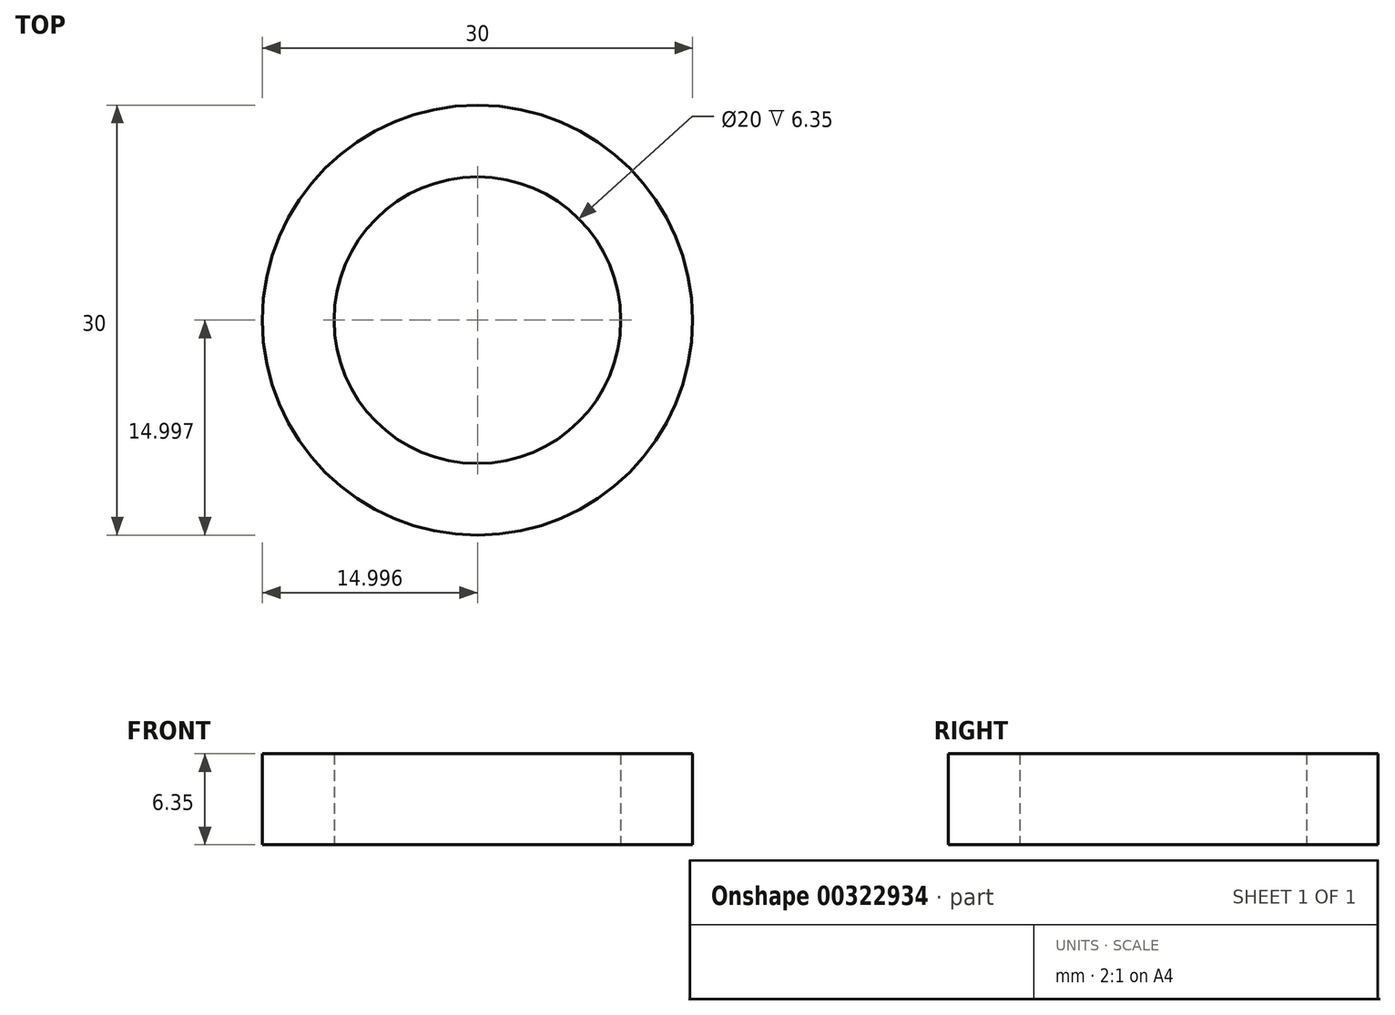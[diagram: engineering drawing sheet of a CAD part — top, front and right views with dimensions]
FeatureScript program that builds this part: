
annotation { "Feature Type Name" : "Feature", "Feature Type Description" : "" }
export const myFeature = defineFeature(function(context is Context, id is Id, definition is map)
    precondition{}
    {
        {
            var Q0;
            Q0=qCreatedBy(makeId("Top.planeOp"),FACE);
            var sketch = newSketch(context, id + "F0", { "sketchPlane" : qUnion([Q0])});
            skCircle(sketch, "E0", {"center": v(-38.05, 38.3) * mm, "radius": 15 * mm});
            skCircle(sketch, "E1", {"center": v(-38.05, 38.3) * mm, "radius": 10 * mm});
            skSolve(sketch);
        }
        {
            var Q0;
            Q0=makeQuery(id+"F0.imprint","IMPRINT",FACE,{"disambiguationData":[TD([[makeQuery(id+"F0.imprint","IMPRINT",EDGE,{"derivedFrom":sQuery(id+"F0.wireOp",EDGE,"E0")}),1.0]])]});
            extrude(context, id + "F1", {"entities" : qUnion([Q0]), "depth" : 6.35 * mm});
        }
    });
